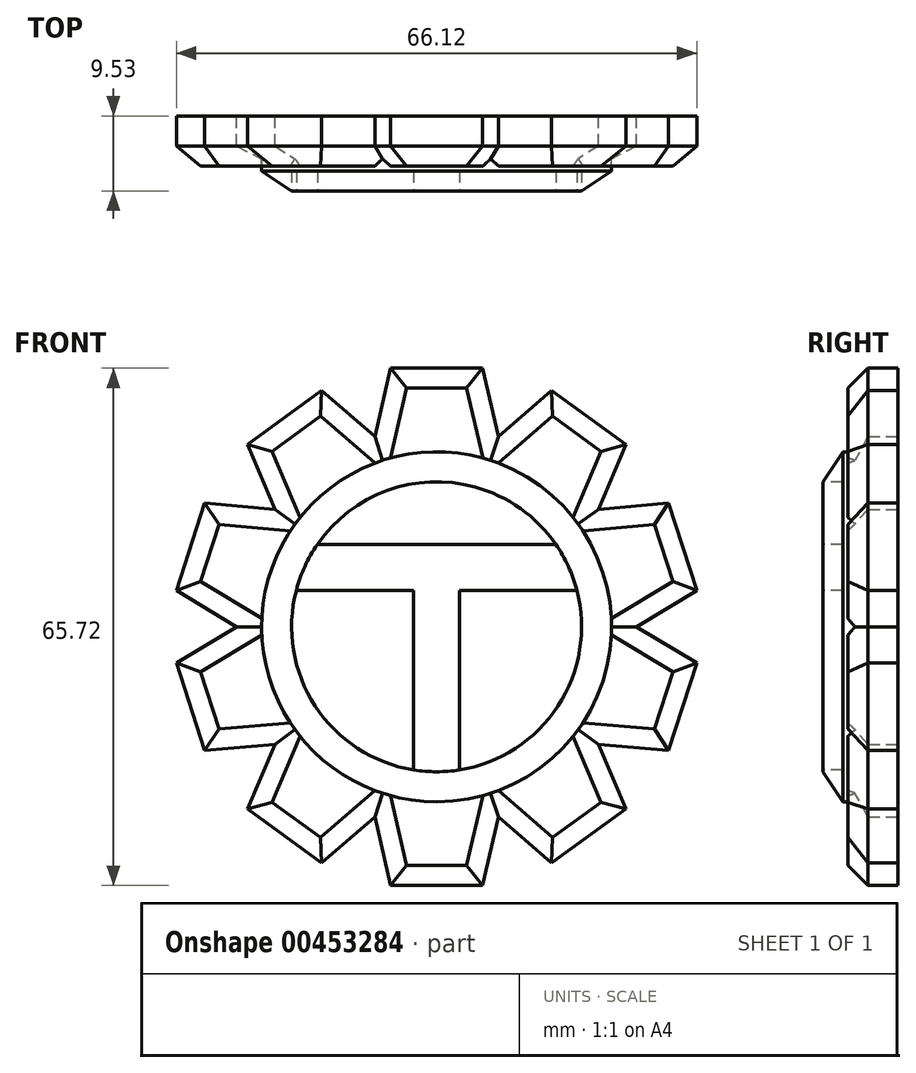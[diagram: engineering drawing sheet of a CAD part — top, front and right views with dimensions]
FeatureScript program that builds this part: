
annotation { "Feature Type Name" : "Feature", "Feature Type Description" : "" }
export const myFeature = defineFeature(function(context is Context, id is Id, definition is map)
    precondition{}
    {
        {
            var Q0;
            Q0=qCreatedBy(makeId("Front.planeOp"),FACE);
            var sketch = newSketch(context, id + "F0", { "sketchPlane" : qUnion([Q0])});
            skCircle(sketch, "E0", {"center": v(0, 0) * mm, "radius": 25.4 * mm});
            skCircle(sketch, "E1.cCircle", {"center": v(0, 0) * mm, "radius": 25.4 * mm, "construction": true});
            skLineSegment(sketch, "E1.0", {"start": v(25.4, 0) * mm, "end": v(20.55, -14.93) * mm, "construction": true});
            skLineSegment(sketch, "E1.1", {"start": v(20.55, -14.93) * mm, "end": v(7.85, -24.16) * mm, "construction": true});
            skLineSegment(sketch, "E1.2", {"start": v(7.85, -24.16) * mm, "end": v(-7.85, -24.16) * mm, "construction": true});
            skLineSegment(sketch, "E1.3", {"start": v(-7.85, -24.16) * mm, "end": v(-20.55, -14.93) * mm, "construction": true});
            skLineSegment(sketch, "E1.4", {"start": v(-20.55, -14.93) * mm, "end": v(-25.4, 0) * mm, "construction": true});
            skLineSegment(sketch, "E1.5", {"start": v(-25.4, 0) * mm, "end": v(-20.55, 14.93) * mm, "construction": true});
            skLineSegment(sketch, "E1.6", {"start": v(-20.55, 14.93) * mm, "end": v(-7.85, 24.16) * mm, "construction": true});
            skLineSegment(sketch, "E1.7", {"start": v(-7.85, 24.16) * mm, "end": v(7.85, 24.16) * mm, "construction": true});
            skLineSegment(sketch, "E1.8", {"start": v(7.85, 24.16) * mm, "end": v(20.55, 14.93) * mm, "construction": true});
            skLineSegment(sketch, "E1.9", {"start": v(20.55, 14.93) * mm, "end": v(25.4, 0) * mm, "construction": true});
            skLineSegment(sketch, "E2", {"start": v(-7.85, 24.16) * mm, "end": v(-5.84, 32.86) * mm});
            skLineSegment(sketch, "E3", {"start": v(-5.84, 32.86) * mm, "end": v(5.84, 32.86) * mm});
            skLineSegment(sketch, "E4", {"start": v(5.84, 32.86) * mm, "end": v(7.85, 24.16) * mm});
            skLineSegment(sketch, "E5.1.0", {"start": v(-20.55, 14.93) * mm, "end": v(-24.04, 23.15) * mm});
            skLineSegment(sketch, "E5.1.1", {"start": v(-24.04, 23.15) * mm, "end": v(-14.59, 30.02) * mm});
            skLineSegment(sketch, "E5.1.2", {"start": v(-14.59, 30.02) * mm, "end": v(-7.85, 24.16) * mm});
            skLineSegment(sketch, "E5.2.0", {"start": v(-25.4, 0) * mm, "end": v(-33.06, 4.6) * mm});
            skLineSegment(sketch, "E5.2.1", {"start": v(-33.06, 4.6) * mm, "end": v(-29.45, 15.7) * mm});
            skLineSegment(sketch, "E5.2.2", {"start": v(-29.45, 15.7) * mm, "end": v(-20.55, 14.93) * mm});
            skLineSegment(sketch, "E5.3.0", {"start": v(-20.55, -14.93) * mm, "end": v(-29.45, -15.7) * mm});
            skLineSegment(sketch, "E5.3.1", {"start": v(-29.45, -15.7) * mm, "end": v(-33.06, -4.6) * mm});
            skLineSegment(sketch, "E5.3.2", {"start": v(-33.06, -4.6) * mm, "end": v(-25.4, 0) * mm});
            skLineSegment(sketch, "E5.4.0", {"start": v(-7.85, -24.16) * mm, "end": v(-14.59, -30.02) * mm});
            skLineSegment(sketch, "E5.4.1", {"start": v(-14.59, -30.02) * mm, "end": v(-24.04, -23.15) * mm});
            skLineSegment(sketch, "E5.4.2", {"start": v(-24.04, -23.15) * mm, "end": v(-20.55, -14.93) * mm});
            skLineSegment(sketch, "E5.5.0", {"start": v(7.85, -24.16) * mm, "end": v(5.84, -32.86) * mm});
            skLineSegment(sketch, "E5.5.1", {"start": v(5.84, -32.86) * mm, "end": v(-5.84, -32.86) * mm});
            skLineSegment(sketch, "E5.5.2", {"start": v(-5.84, -32.86) * mm, "end": v(-7.85, -24.16) * mm});
            skLineSegment(sketch, "E5.6.0", {"start": v(20.55, -14.93) * mm, "end": v(24.04, -23.15) * mm});
            skLineSegment(sketch, "E5.6.1", {"start": v(24.04, -23.15) * mm, "end": v(14.59, -30.02) * mm});
            skLineSegment(sketch, "E5.6.2", {"start": v(14.59, -30.02) * mm, "end": v(7.85, -24.16) * mm});
            skLineSegment(sketch, "E5.7.0", {"start": v(25.4, 0) * mm, "end": v(33.06, -4.6) * mm});
            skLineSegment(sketch, "E5.7.1", {"start": v(33.06, -4.6) * mm, "end": v(29.45, -15.7) * mm});
            skLineSegment(sketch, "E5.7.2", {"start": v(29.45, -15.7) * mm, "end": v(20.55, -14.93) * mm});
            skLineSegment(sketch, "E5.8.0", {"start": v(20.55, 14.93) * mm, "end": v(29.45, 15.7) * mm});
            skLineSegment(sketch, "E5.8.1", {"start": v(29.45, 15.7) * mm, "end": v(33.06, 4.6) * mm});
            skLineSegment(sketch, "E5.8.2", {"start": v(33.06, 4.6) * mm, "end": v(25.4, 0) * mm});
            skLineSegment(sketch, "E5.9.0", {"start": v(7.85, 24.16) * mm, "end": v(14.59, 30.02) * mm});
            skLineSegment(sketch, "E5.9.1", {"start": v(14.59, 30.02) * mm, "end": v(24.04, 23.15) * mm});
            skLineSegment(sketch, "E5.9.2", {"start": v(24.04, 23.15) * mm, "end": v(20.55, 14.93) * mm});
            skSolve(sketch);
        }
        {
            var Q0;
            Q0 = qSketchRegion(id + "F0", true);
            extrude(context, id + "F1", {"entities" : qUnion([Q0]), "depth" : 6.35 * mm});
        }
        {
            var Q0;
            Q0=makeQuery(id+"F1.opExtrude","CAP_FACE",FACE,{"disambiguationData":[OSD([sQuery(id+"F0.wireOp",EDGE,"E2"),sQuery(id+"F0.wireOp",EDGE,"E3"),sQuery(id+"F0.wireOp",EDGE,"E4"),sQuery(id+"F0.wireOp",EDGE,"E5.1.0"),sQuery(id+"F0.wireOp",EDGE,"E5.1.1"),sQuery(id+"F0.wireOp",EDGE,"E5.1.2"),sQuery(id+"F0.wireOp",EDGE,"E5.2.0"),sQuery(id+"F0.wireOp",EDGE,"E5.2.1"),sQuery(id+"F0.wireOp",EDGE,"E5.2.2"),sQuery(id+"F0.wireOp",EDGE,"E5.3.0"),sQuery(id+"F0.wireOp",EDGE,"E5.3.1"),sQuery(id+"F0.wireOp",EDGE,"E5.3.2"),sQuery(id+"F0.wireOp",EDGE,"E5.4.0"),sQuery(id+"F0.wireOp",EDGE,"E5.4.1"),sQuery(id+"F0.wireOp",EDGE,"E5.4.2"),sQuery(id+"F0.wireOp",EDGE,"E5.5.0"),sQuery(id+"F0.wireOp",EDGE,"E5.5.1"),sQuery(id+"F0.wireOp",EDGE,"E5.5.2"),sQuery(id+"F0.wireOp",EDGE,"E5.6.0"),sQuery(id+"F0.wireOp",EDGE,"E5.6.1"),sQuery(id+"F0.wireOp",EDGE,"E5.6.2"),sQuery(id+"F0.wireOp",EDGE,"E5.7.0"),sQuery(id+"F0.wireOp",EDGE,"E5.7.1"),sQuery(id+"F0.wireOp",EDGE,"E5.7.2"),sQuery(id+"F0.wireOp",EDGE,"E5.8.0"),sQuery(id+"F0.wireOp",EDGE,"E5.8.1"),sQuery(id+"F0.wireOp",EDGE,"E5.8.2"),sQuery(id+"F0.wireOp",EDGE,"E5.9.0"),sQuery(id+"F0.wireOp",EDGE,"E5.9.1"),sQuery(id+"F0.wireOp",EDGE,"E5.9.2")])],"isStart":false});
            chamfer(context, id + "F2", {"entities" : qUnion([Q0]), "width" : 2.54 * mm, "tangentPropagation" : true});
        }
        {
            var Q0;
            Q0=makeQuery(id+"F1.opExtrude","CAP_FACE",FACE,{"disambiguationData":[OSD([sQuery(id+"F0.wireOp",EDGE,"E2"),sQuery(id+"F0.wireOp",EDGE,"E3"),sQuery(id+"F0.wireOp",EDGE,"E4"),sQuery(id+"F0.wireOp",EDGE,"E5.1.0"),sQuery(id+"F0.wireOp",EDGE,"E5.1.1"),sQuery(id+"F0.wireOp",EDGE,"E5.1.2"),sQuery(id+"F0.wireOp",EDGE,"E5.2.0"),sQuery(id+"F0.wireOp",EDGE,"E5.2.1"),sQuery(id+"F0.wireOp",EDGE,"E5.2.2"),sQuery(id+"F0.wireOp",EDGE,"E5.3.0"),sQuery(id+"F0.wireOp",EDGE,"E5.3.1"),sQuery(id+"F0.wireOp",EDGE,"E5.3.2"),sQuery(id+"F0.wireOp",EDGE,"E5.4.0"),sQuery(id+"F0.wireOp",EDGE,"E5.4.1"),sQuery(id+"F0.wireOp",EDGE,"E5.4.2"),sQuery(id+"F0.wireOp",EDGE,"E5.5.0"),sQuery(id+"F0.wireOp",EDGE,"E5.5.1"),sQuery(id+"F0.wireOp",EDGE,"E5.5.2"),sQuery(id+"F0.wireOp",EDGE,"E5.6.0"),sQuery(id+"F0.wireOp",EDGE,"E5.6.1"),sQuery(id+"F0.wireOp",EDGE,"E5.6.2"),sQuery(id+"F0.wireOp",EDGE,"E5.7.0"),sQuery(id+"F0.wireOp",EDGE,"E5.7.1"),sQuery(id+"F0.wireOp",EDGE,"E5.7.2"),sQuery(id+"F0.wireOp",EDGE,"E5.8.0"),sQuery(id+"F0.wireOp",EDGE,"E5.8.1"),sQuery(id+"F0.wireOp",EDGE,"E5.8.2"),sQuery(id+"F0.wireOp",EDGE,"E5.9.0"),sQuery(id+"F0.wireOp",EDGE,"E5.9.1"),sQuery(id+"F0.wireOp",EDGE,"E5.9.2")])],"isStart":false});
            var sketch = newSketch(context, id + "F3", { "sketchPlane" : qUnion([Q0])});
            skCircle(sketch, "E6", {"center": v(0, 0) * mm, "radius": 22.23 * mm});
            skSolve(sketch);
        }
        {
            var Q0;
            Q0 = qSketchRegion(id + "F3", true);
            extrude(context, id + "F4", {"entities" : qUnion([Q0]), "operationType" : NewBodyOperationType.ADD, "endBound" : BoundingType.SYMMETRIC, "depth" : 6.35 * mm});
        }
        {
            var Q0;
            Q0=makeQuery(id+"F4.opExtrude","CAP_EDGE",EDGE,{"disambiguationData":[OSD([sQuery(id+"F3.wireOp",EDGE,"E6")])],"isStart":false});
            chamfer(context, id + "F5", {"entities" : qUnion([Q0]), "chamferType" : ChamferType.TWO_OFFSETS, "width1" : 3.8 * mm, "oppositeDirection" : false, "width2" : 2.54 * mm, "tangentPropagation" : true});
        }
        {
            var Q0;
            Q0=makeQuery(id+"F4.opExtrude","CAP_FACE",FACE,{"disambiguationData":[OSD([sQuery(id+"F3.wireOp",EDGE,"E6")])],"isStart":false});
            var sketch = newSketch(context, id + "F6", { "sketchPlane" : qUnion([Q0])});
            skLineSegment(sketch, "E7", {"start": v(-17.82, 4.65) * mm, "end": v(-2.92, 4.65) * mm});
            skLineSegment(sketch, "E8", {"start": v(-15.14, 10.49) * mm, "end": v(15.14, 10.49) * mm});
            skLineSegment(sketch, "E9.bottom", {"start": v(2.92, -18.18) * mm, "end": v(-2.92, -18.18) * mm});
            skLineSegment(sketch, "E9.left", {"start": v(2.92, -18.18) * mm, "end": v(2.92, 4.88) * mm});
            skLineSegment(sketch, "E9.right", {"start": v(-2.92, -18.18) * mm, "end": v(-2.92, 4.88) * mm});
            skPoint(sketch, "E9.middle", {"position": v(0, -6.65) * mm});
            skLineSegment(sketch, "E10.trimOffspring", {"start": v(2.92, 4.65) * mm, "end": v(17.82, 4.65) * mm});
            skSolve(sketch);
        }
        {
            var Q0;
            Q0 = qSketchRegion(id + "F6", true);
            var Q1;
            {var subQ0=sQuery(id+"F6.wireOp",EDGE,"E7");Q1=makeQuery(id+"F6.imprint","IMPRINT",FACE,{"disambiguationData":[TD([[makeQuery(id+"F6.imprint","IMPRINT",EDGE,{"derivedFrom":subQ0}),-1.0]])]});}
            var Q2;
            {var subQ0=sQuery(id+"F6.wireOp",EDGE,"E8");Q2=makeQuery(id+"F6.imprint","IMPRINT",FACE,{"disambiguationData":[TD([[makeQuery(id+"F6.imprint","IMPRINT",EDGE,{"derivedFrom":subQ0}),1.0]])]});}
            var Q3;
            {var subQ4=sQuery(id+"F6.wireOp",EDGE,"E10.trimOffspring");Q3=makeQuery(id+"F6.imprint","IMPRINT",FACE,{"disambiguationData":[TD([[makeQuery(id+"F6.imprint","IMPRINT",EDGE,{"derivedFrom":subQ4}),-1.0]])]});}
            extrude(context, id + "F7", {"entities" : qUnion([Q0, Q1, Q2, Q3]), "operationType" : NewBodyOperationType.REMOVE, "oppositeDirection" : true, "depth" : 2.54 * mm});
        }
    });
